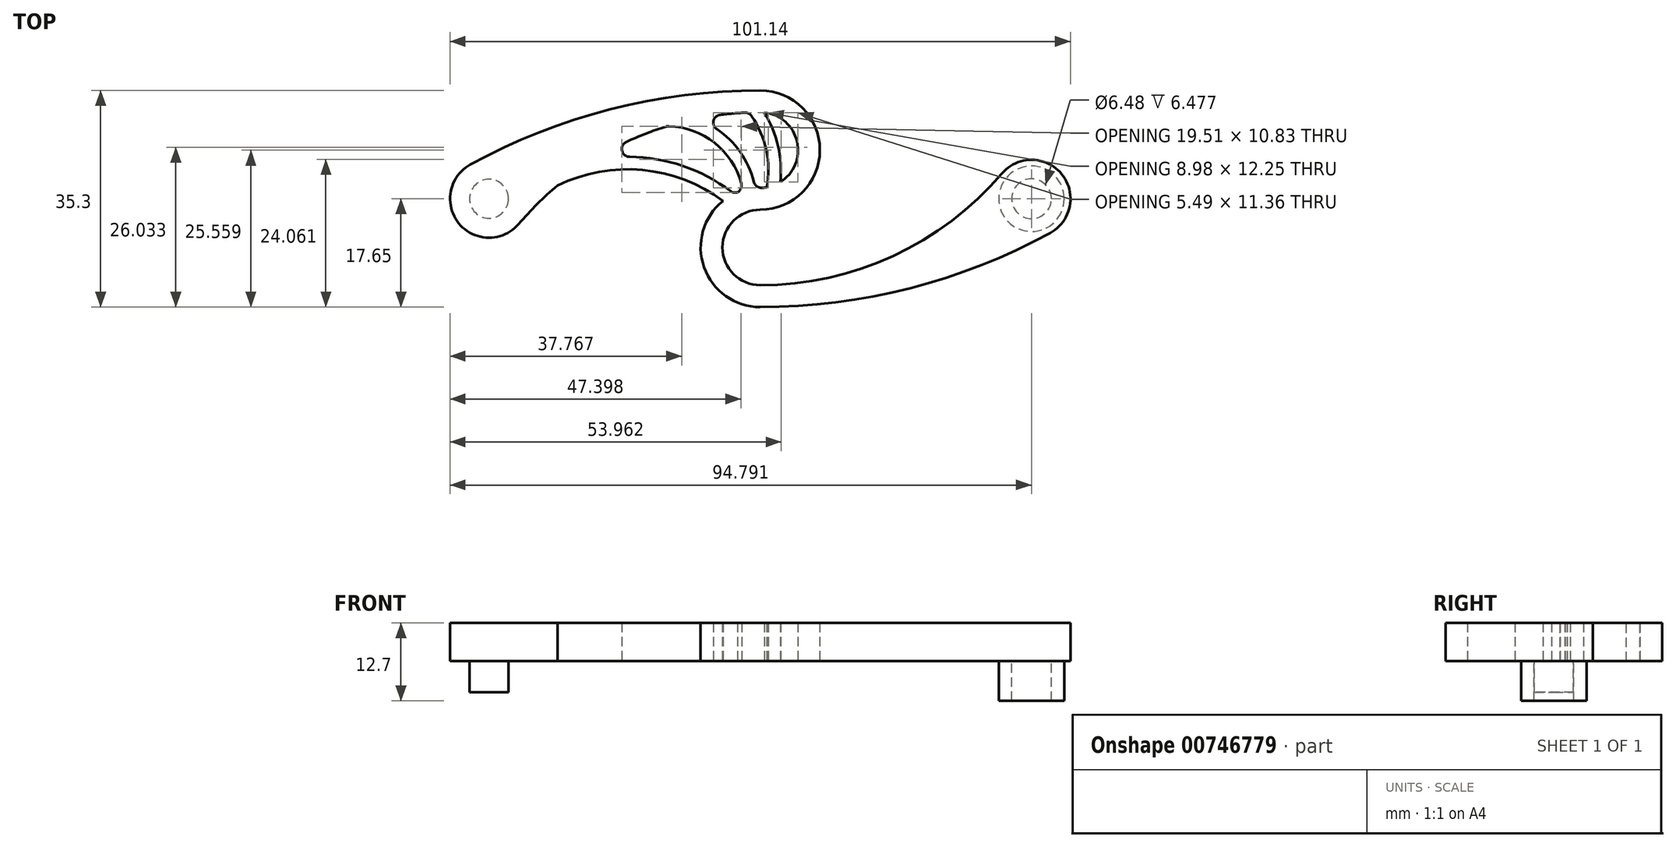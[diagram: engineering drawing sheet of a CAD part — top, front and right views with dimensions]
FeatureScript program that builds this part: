
annotation { "Feature Type Name" : "Feature", "Feature Type Description" : "" }
export const myFeature = defineFeature(function(context is Context, id is Id, definition is map)
    precondition{}
    {
        {
            var Q0;
            Q0=qCreatedBy(makeId("Top.planeOp"),FACE);
            var sketch = newSketch(context, id + "F0", { "sketchPlane" : qUnion([Q0])});
            skArc(sketch, "E0", {"start": v(0, 0) * mm, "mid": v(7.94, 7.94) * mm, "end": v(0, 15.87) * mm, "construction": true});
            skArc(sketch, "E1", {"start": v(0, 15.87) * mm, "mid": v(-23.5, 11.79) * mm, "end": v(-44.22, 0) * mm, "construction": true});
            skArc(sketch, "E2", {"start": v(0, 0) * mm, "mid": v(-7.94, -7.94) * mm, "end": v(0, -15.87) * mm, "construction": true});
            skArc(sketch, "E3", {"start": v(0, -15.88) * mm, "mid": v(23.5, -11.79) * mm, "end": v(44.22, 0) * mm, "construction": true});
            skLineSegment(sketch, "E4", {"start": v(0, -24.33) * mm, "end": v(0, 27.89) * mm, "construction": true});
            skCircle(sketch, "E5", {"center": v(-44.22, 0) * mm, "radius": 6.35 * mm});
            skCircle(sketch, "E6", {"center": v(44.22, 0) * mm, "radius": 6.35 * mm});
            skArc(sketch, "E7", {"start": v(0, 17.65) * mm, "mid": v(-24.4, 14.58) * mm, "end": v(-47.27, 5.57) * mm});
            skArc(sketch, "E8", {"start": v(0, -1.78) * mm, "mid": v(9.72, 7.94) * mm, "end": v(0, 17.65) * mm});
            skArc(sketch, "E9", {"start": v(0, -1.78) * mm, "mid": v(-6.16, -7.94) * mm, "end": v(0, -14.1) * mm});
            skLineSegment(sketch, "E10", {"start": v(-25.3, 0) * mm, "end": v(14.92, 0) * mm, "construction": true});
            skArc(sketch, "E11", {"start": v(0, -14.1) * mm, "mid": v(21.7, -9.32) * mm, "end": v(39.38, 4.11) * mm});
            skArc(sketch, "E12", {"start": v(0, 14.1) * mm, "mid": v(-21.7, 9.32) * mm, "end": v(-39.38, -4.11) * mm});
            skArc(sketch, "E13", {"start": v(0, 1.78) * mm, "mid": v(6.16, 7.94) * mm, "end": v(0, 14.1) * mm});
            skArc(sketch, "E14", {"start": v(0, 1.78) * mm, "mid": v(-9.72, -7.94) * mm, "end": v(0, -17.65) * mm});
            skArc(sketch, "E15", {"start": v(0, -17.65) * mm, "mid": v(24.4, -14.58) * mm, "end": v(47.27, -5.57) * mm});
            skCircle(sketch, "E16", {"center": v(-44.22, 0) * mm, "radius": 3.18 * mm});
            skCircle(sketch, "E17", {"center": v(44.22, 0) * mm, "radius": 5.33 * mm});
            skCircle(sketch, "E18", {"center": v(44.22, 0) * mm, "radius": 3.24 * mm});
            skArc(sketch, "E19", {"start": v(1.07, 1.87) * mm, "mid": v(0.9, 8.27) * mm, "end": v(-1.82, 14.06) * mm});
            skArc(sketch, "E20.0", {"start": v(3.24, 2.7) * mm, "mid": v(2.9, 8.6) * mm, "end": v(0.65, 14.06) * mm});
            skArc(sketch, "E21", {"start": v(-6.09, -0.36) * mm, "mid": v(-19.21, 4.7) * mm, "end": v(-33.05, 2.15) * mm});
            skArc(sketch, "E22.0", {"start": v(-4.26, 0.8) * mm, "mid": v(-15.22, 6.1) * mm, "end": v(-27.4, 6.23) * mm});
            skArc(sketch, "E23", {"start": v(-2.83, 1.36) * mm, "mid": v(-7.1, 8.81) * mm, "end": v(-15.13, 11.83) * mm});
            skArc(sketch, "E24.0", {"start": v(-0.84, 1.74) * mm, "mid": v(-4.1, 8.69) * mm, "end": v(-10.43, 13.03) * mm});
            skSolve(sketch);
        }
        {
            var Q0;
            {var subQ0=sQuery(id+"F0.wireOp",EDGE,"E5");var subQ1=makeQuery(id+"F0.imprint","INTERSECT",VERTEX,{"derivedFrom":[subQ0,sQuery(id+"F0.wireOp",EDGE,"E7")]});Q0=makeQuery(id+"F0.imprint","IMPRINT",FACE,{"disambiguationData":[TD([[makeQuery(id+"F0.imprint","IMPRINT",EDGE,{"disambiguationData":[TD([[subQ1,-1.0]])],"derivedFrom":subQ0}),1.0]])]});}
            var Q1;
            {var subQ0=sQuery(id+"F0.wireOp",EDGE,"E7");Q1=makeQuery(id+"F0.imprint","IMPRINT",FACE,{"disambiguationData":[TD([[makeQuery(id+"F0.imprint","IMPRINT",EDGE,{"derivedFrom":subQ0}),1.0]])]});}
            var Q2;
            {var subQ0=sQuery(id+"F0.wireOp",EDGE,"E6");var subQ1=makeQuery(id+"F0.imprint","INTERSECT",VERTEX,{"derivedFrom":[subQ0,sQuery(id+"F0.wireOp",EDGE,"E11")]});Q2=makeQuery(id+"F0.imprint","IMPRINT",FACE,{"disambiguationData":[TD([[makeQuery(id+"F0.imprint","IMPRINT",EDGE,{"disambiguationData":[TD([[subQ1,-1.0]])],"derivedFrom":subQ0}),1.0]])]});}
            var Q3;
            Q3=makeQuery(id+"F0.imprint","IMPRINT",FACE,{"disambiguationData":[TD([[makeQuery(id+"F0.imprint","IMPRINT",EDGE,{"derivedFrom":sQuery(id+"F0.wireOp",EDGE,"E16")}),1.0]])]});
            var Q4;
            Q4=makeQuery(id+"F0.imprint","IMPRINT",FACE,{"disambiguationData":[TD([[makeQuery(id+"F0.imprint","IMPRINT",EDGE,{"derivedFrom":sQuery(id+"F0.wireOp",EDGE,"E17")}),1.0]])]});
            var Q5;
            Q5=makeQuery(id+"F0.imprint","IMPRINT",FACE,{"disambiguationData":[TD([[makeQuery(id+"F0.imprint","IMPRINT",EDGE,{"derivedFrom":sQuery(id+"F0.wireOp",EDGE,"E18")}),1.0]])]});
            extrude(context, id + "F1", {"entities" : qUnion([Q0, Q1, Q2, Q3, Q4, Q5]), "depth" : 6.22 * mm, "offsetDistance" : 25.4 * mm});
        }
        {
            var Q0;
            Q0=makeQuery(id+"F0.imprint","IMPRINT",FACE,{"disambiguationData":[TD([[makeQuery(id+"F0.imprint","IMPRINT",EDGE,{"derivedFrom":sQuery(id+"F0.wireOp",EDGE,"E16")}),1.0]])]});
            extrude(context, id + "F2", {"entities" : qUnion([Q0]), "operationType" : NewBodyOperationType.ADD, "oppositeDirection" : true, "depth" : 5.08 * mm, "offsetDistance" : 25.4 * mm});
        }
        {
            var Q0;
            Q0=makeQuery(id+"F0.imprint","IMPRINT",FACE,{"disambiguationData":[TD([[makeQuery(id+"F0.imprint","IMPRINT",EDGE,{"derivedFrom":sQuery(id+"F0.wireOp",EDGE,"E17")}),1.0]])]});
            extrude(context, id + "F3", {"entities" : qUnion([Q0]), "operationType" : NewBodyOperationType.ADD, "oppositeDirection" : true, "depth" : 6.48 * mm, "offsetDistance" : 25.4 * mm});
        }
        {
            var Q0;
            {var subQ0=sQuery(id+"F0.wireOp",EDGE,"E19");Q0=makeQuery(id+"F0.imprint","IMPRINT",FACE,{"disambiguationData":[TD([[makeQuery(id+"F0.imprint","IMPRINT",EDGE,{"derivedFrom":subQ0}),-1.0]])]});}
            var Q1;
            {var subQ0=sQuery(id+"F0.wireOp",EDGE,"0I1vGfar-pBzT-Gtq0-xfIU-gbTXO5mySZYQ");Q1=makeQuery(id+"F0.imprint","IMPRINT",FACE,{"disambiguationData":[TD([[makeQuery(id+"F0.imprint","IMPRINT",EDGE,{"derivedFrom":subQ0}),-1.0]])]});}
            var Q2;
            {var subQ0=sQuery(id+"F0.wireOp",EDGE,"E21");Q2=makeQuery(id+"F0.imprint","IMPRINT",FACE,{"disambiguationData":[TD([[makeQuery(id+"F0.imprint","IMPRINT",EDGE,{"derivedFrom":subQ0}),-1.0]])]});}
            var Q3;
            {var subQ0=sQuery(id+"F0.wireOp",EDGE,"E23");Q3=makeQuery(id+"F0.imprint","IMPRINT",FACE,{"disambiguationData":[TD([[makeQuery(id+"F0.imprint","IMPRINT",EDGE,{"derivedFrom":subQ0}),-1.0]])]});}
            var Q4;
            Q4=makeQuery(id+"F1.opExtrude","CAP_FACE",FACE,{"disambiguationData":[OSD([sQuery(id+"F0.wireOp",EDGE,"E5"),sQuery(id+"F0.wireOp",EDGE,"E6"),sQuery(id+"F0.wireOp",EDGE,"E7"),sQuery(id+"F0.wireOp",EDGE,"E8"),sQuery(id+"F0.wireOp",EDGE,"E9"),sQuery(id+"F0.wireOp",EDGE,"E11"),sQuery(id+"F0.wireOp",EDGE,"E12"),sQuery(id+"F0.wireOp",EDGE,"E13"),sQuery(id+"F0.wireOp",EDGE,"E14"),sQuery(id+"F0.wireOp",EDGE,"E15")])],"isStart":false});
            extrude(context, id + "F4", {"entities" : qUnion([Q0, Q1, Q2, Q3]), "operationType" : NewBodyOperationType.ADD, "endBound" : BoundingType.UP_TO_SURFACE, "depth" : 25.4 * mm, "endBoundEntityFace" : qUnion([Q4]), "offsetDistance" : 25.4 * mm});
        }
        {
            var Q0;
            Q0=qCreatedBy(makeId("Right.planeOp"),FACE);
            var sketch = newSketch(context, id + "F5", { "sketchPlane" : qUnion([Q0])});
            skLineSegment(sketch, "E25", {"start": v(0, 0) * mm, "end": v(0, 59.16) * mm, "construction": true});
            skSolve(sketch);
        }
        {
            var Q0;
            Q0=makeQuery(id+"FfAuDH6qegAbosX_1.1.F4.opExtrude","SWEPT_EDGE",EDGE,{"disambiguationData":[OSD([sQuery(id+"F0.wireOp",EDGE,"E12"),sQuery(id+"F0.wireOp",EDGE,"E21")])]});
            var Q1;
            Q1=makeQuery(id+"FfAuDH6qegAbosX_1.1.F4.opExtrude","SWEPT_EDGE",EDGE,{"disambiguationData":[OSD([sQuery(id+"F0.wireOp",EDGE,"E12"),sQuery(id+"F0.wireOp",EDGE,"E23")])]});
            var Q2;
            Q2=makeQuery(id+"FfAuDH6qegAbosX_1.1.F4.opExtrude","SWEPT_EDGE",EDGE,{"disambiguationData":[OSD([sQuery(id+"F0.wireOp",EDGE,"E12"),sQuery(id+"F0.wireOp",EDGE,"E19")])]});
            var Q3;
            {var subQ0=sQuery(id+"F0.wireOp",EDGE,"E20.0");var subQ1=sQuery(id+"F0.wireOp",EDGE,"E13");Q3=makeQuery(id+"FfAuDH6qegAbosX_1.1.F4.opExtrude","SWEPT_EDGE",EDGE,{"disambiguationData":[OSD([subQ1,subQ0]),TDD([makeQuery(id+"F0.imprint","INTERSECT",VERTEX,{"disambiguationData":[OD(1.0)],"derivedFrom":[subQ1,subQ0]})])]});}
            var Q4;
            {var subQ0=sQuery(id+"F0.wireOp",EDGE,"E20.0");var subQ1=sQuery(id+"F0.wireOp",EDGE,"E13");Q4=makeQuery(id+"FfAuDH6qegAbosX_1.1.F4.opExtrude","SWEPT_EDGE",EDGE,{"disambiguationData":[OSD([subQ1,subQ0]),TDD([makeQuery(id+"F0.imprint","INTERSECT",VERTEX,{"disambiguationData":[OD(0.0)],"derivedFrom":[subQ1,subQ0]})])]});}
            var Q5;
            Q5=makeQuery(id+"FfAuDH6qegAbosX_1.1.F4.opExtrude","SWEPT_EDGE",EDGE,{"disambiguationData":[OSD([sQuery(id+"F0.wireOp",EDGE,"E13"),sQuery(id+"F0.wireOp",EDGE,"E19")])]});
            var Q6;
            Q6=makeQuery(id+"FfAuDH6qegAbosX_1.1.F4.opExtrude","SWEPT_EDGE",EDGE,{"disambiguationData":[OSD([sQuery(id+"F0.wireOp",EDGE,"E14"),sQuery(id+"F0.wireOp",EDGE,"E24.0")])]});
            var Q7;
            Q7=makeQuery(id+"FfAuDH6qegAbosX_1.1.F4.opExtrude","SWEPT_EDGE",EDGE,{"disambiguationData":[OSD([sQuery(id+"F0.wireOp",EDGE,"E14"),sQuery(id+"F0.wireOp",EDGE,"E23")])]});
            var Q8;
            Q8=makeQuery(id+"FfAuDH6qegAbosX_1.1.F4.opExtrude","SWEPT_EDGE",EDGE,{"disambiguationData":[OSD([sQuery(id+"F0.wireOp",EDGE,"E14"),sQuery(id+"F0.wireOp",EDGE,"E22.0")])]});
            var Q9;
            {var subQ0=sQuery(id+"F0.wireOp",EDGE,"E20.0");var subQ1=sQuery(id+"F0.wireOp",EDGE,"E13");Q9=makeQuery(id+"F4.opExtrude","SWEPT_EDGE",EDGE,{"disambiguationData":[OSD([subQ1,subQ0]),TDD([makeQuery(id+"F0.imprint","INTERSECT",VERTEX,{"disambiguationData":[OD(1.0)],"derivedFrom":[subQ1,subQ0]})])]});}
            var Q10;
            {var subQ0=sQuery(id+"F0.wireOp",EDGE,"E20.0");var subQ1=sQuery(id+"F0.wireOp",EDGE,"E13");Q10=makeQuery(id+"F4.opExtrude","SWEPT_EDGE",EDGE,{"disambiguationData":[OSD([subQ1,subQ0]),TDD([makeQuery(id+"F0.imprint","INTERSECT",VERTEX,{"disambiguationData":[OD(0.0)],"derivedFrom":[subQ1,subQ0]})])]});}
            var Q11;
            Q11=makeQuery(id+"F4.opExtrude","SWEPT_EDGE",EDGE,{"disambiguationData":[OSD([sQuery(id+"F0.wireOp",EDGE,"E14"),sQuery(id+"F0.wireOp",EDGE,"E24.0")])]});
            var Q12;
            Q12=makeQuery(id+"F4.opExtrude","SWEPT_EDGE",EDGE,{"disambiguationData":[OSD([sQuery(id+"F0.wireOp",EDGE,"E12"),sQuery(id+"F0.wireOp",EDGE,"E24.0")])]});
            var Q13;
            Q13=makeQuery(id+"F4.opExtrude","SWEPT_EDGE",EDGE,{"disambiguationData":[OSD([sQuery(id+"F0.wireOp",EDGE,"E12"),sQuery(id+"F0.wireOp",EDGE,"E22.0")])]});
            var Q14;
            Q14=makeQuery(id+"F4.opExtrude","SWEPT_EDGE",EDGE,{"disambiguationData":[OSD([sQuery(id+"F0.wireOp",EDGE,"E14"),sQuery(id+"F0.wireOp",EDGE,"E23")])]});
            var Q15;
            Q15=makeQuery(id+"F4.opExtrude","SWEPT_EDGE",EDGE,{"disambiguationData":[OSD([sQuery(id+"F0.wireOp",EDGE,"E14"),sQuery(id+"F0.wireOp",EDGE,"E22.0")])]});
            var Q16;
            Q16=makeQuery(id+"FfAuDH6qegAbosX_1.1.F4.opExtrude","SWEPT_EDGE",EDGE,{"disambiguationData":[OSD([sQuery(id+"F0.wireOp",EDGE,"E12"),sQuery(id+"F0.wireOp",EDGE,"E22.0")])]});
            var Q17;
            Q17=makeQuery(id+"F4.opExtrude","SWEPT_EDGE",EDGE,{"disambiguationData":[OSD([sQuery(id+"F0.wireOp",EDGE,"E12"),sQuery(id+"F0.wireOp",EDGE,"E21")])]});
            var Q18;
            Q18=makeQuery(id+"F4.opExtrude","SWEPT_EDGE",EDGE,{"disambiguationData":[OSD([sQuery(id+"F0.wireOp",EDGE,"E12"),sQuery(id+"F0.wireOp",EDGE,"E23")])]});
            var Q19;
            Q19=makeQuery(id+"F4.opExtrude","SWEPT_EDGE",EDGE,{"disambiguationData":[OSD([sQuery(id+"F0.wireOp",EDGE,"E12"),sQuery(id+"F0.wireOp",EDGE,"E19")])]});
            fillet(context, id + "F6", {"entities" : qUnion([Q0, Q1, Q2, Q3, Q4, Q5, Q6, Q7, Q8, Q9, Q10, Q11, Q12, Q13, Q14, Q15, Q16, Q17, Q18, Q19]), "tangentPropagation" : true, "radius" : 1.27 * mm, "defaultsChanged" : false, "vertexSettings" : [], "allowEdgeOverflow" : false});
        }
    });
